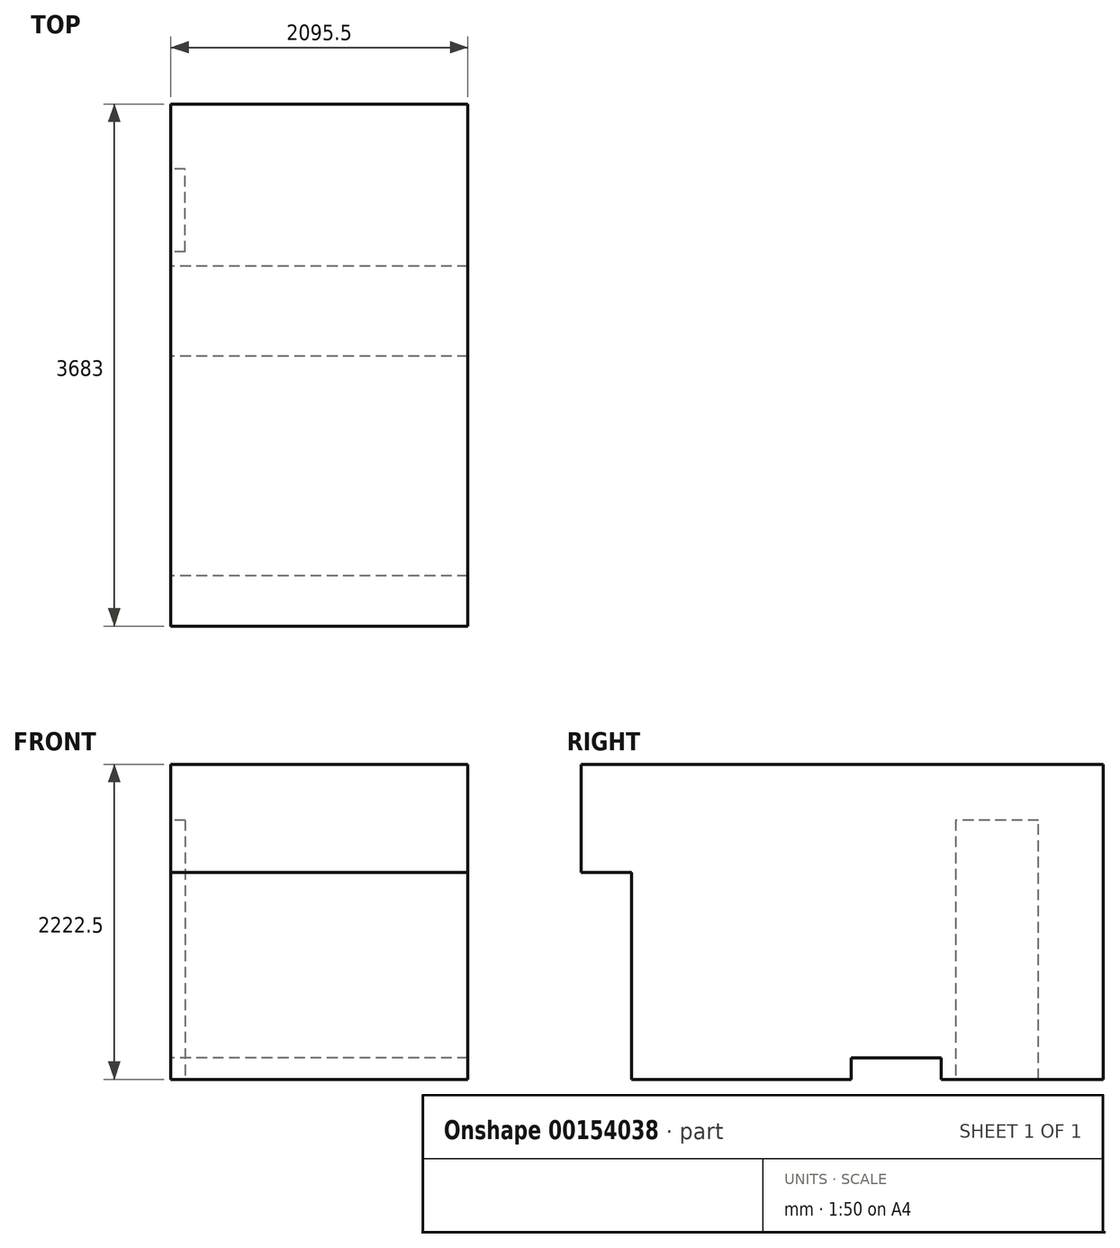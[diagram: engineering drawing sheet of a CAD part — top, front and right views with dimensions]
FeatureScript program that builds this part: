
annotation { "Feature Type Name" : "Feature", "Feature Type Description" : "" }
export const myFeature = defineFeature(function(context is Context, id is Id, definition is map)
    precondition{}
    {
        {
            var Q0;
            Q0=qCreatedBy(makeId("Right.planeOp"),FACE);
            var sketch = newSketch(context, id + "F0", { "sketchPlane" : qUnion([Q0])});
            skLineSegment(sketch, "E0", {"start": v(0, 0) * mm, "end": v(3327.4, 0) * mm});
            skLineSegment(sketch, "E1", {"start": v(3327.4, 0) * mm, "end": v(3327.4, 2222.5) * mm});
            skLineSegment(sketch, "E2", {"start": v(3327.4, 2222.5) * mm, "end": v(-355.6, 2222.5) * mm});
            skLineSegment(sketch, "E3", {"start": v(-355.6, 2222.5) * mm, "end": v(-355.6, 1460.5) * mm});
            skLineSegment(sketch, "E4", {"start": v(-355.6, 1460.5) * mm, "end": v(0, 1460.5) * mm});
            skLineSegment(sketch, "E5", {"start": v(0, 1460.5) * mm, "end": v(0, 0) * mm});
            skLineSegment(sketch, "E6", {"start": v(2870.2, 0) * mm, "end": v(2870.2, 1828.8) * mm});
            skLineSegment(sketch, "E7", {"start": v(2870.2, 1828.8) * mm, "end": v(2286, 1828.8) * mm});
            skLineSegment(sketch, "E8", {"start": v(2286, 1828.8) * mm, "end": v(2286, 0) * mm});
            skLineSegment(sketch, "E9", {"start": v(2184.4, 0) * mm, "end": v(2184.4, 152.4) * mm});
            skLineSegment(sketch, "E10", {"start": v(2184.4, 152.4) * mm, "end": v(1549.4, 152.4) * mm});
            skLineSegment(sketch, "E11", {"start": v(1549.4, 152.4) * mm, "end": v(1549.4, 0) * mm});
            skSolve(sketch);
        }
        {
            var Q0;
            {var subQ6=sQuery(id+"F0.wireOp",EDGE,"E1");Q0=makeQuery(id+"F0.imprint","IMPRINT",FACE,{"disambiguationData":[TD([[makeQuery(id+"F0.imprint","IMPRINT",EDGE,{"derivedFrom":subQ6}),1.0]])]});}
            var Q1;
            {var subQ0=sQuery(id+"F0.wireOp",EDGE,"E6");Q1=makeQuery(id+"F0.imprint","IMPRINT",FACE,{"disambiguationData":[TD([[makeQuery(id+"F0.imprint","IMPRINT",EDGE,{"derivedFrom":subQ0}),1.0]])]});}
            extrude(context, id + "F1", {"entities" : qUnion([Q0, Q1]), "depth" : 2095.5 * mm});
        }
        {
            var Q0;
            {var subQ0=sQuery(id+"F0.wireOp",EDGE,"E6");Q0=makeQuery(id+"F0.imprint","IMPRINT",FACE,{"disambiguationData":[TD([[makeQuery(id+"F0.imprint","IMPRINT",EDGE,{"derivedFrom":subQ0}),1.0]])]});}
            extrude(context, id + "F2", {"entities" : qUnion([Q0]), "operationType" : NewBodyOperationType.REMOVE, "depth" : 101.6 * mm});
        }
    });
